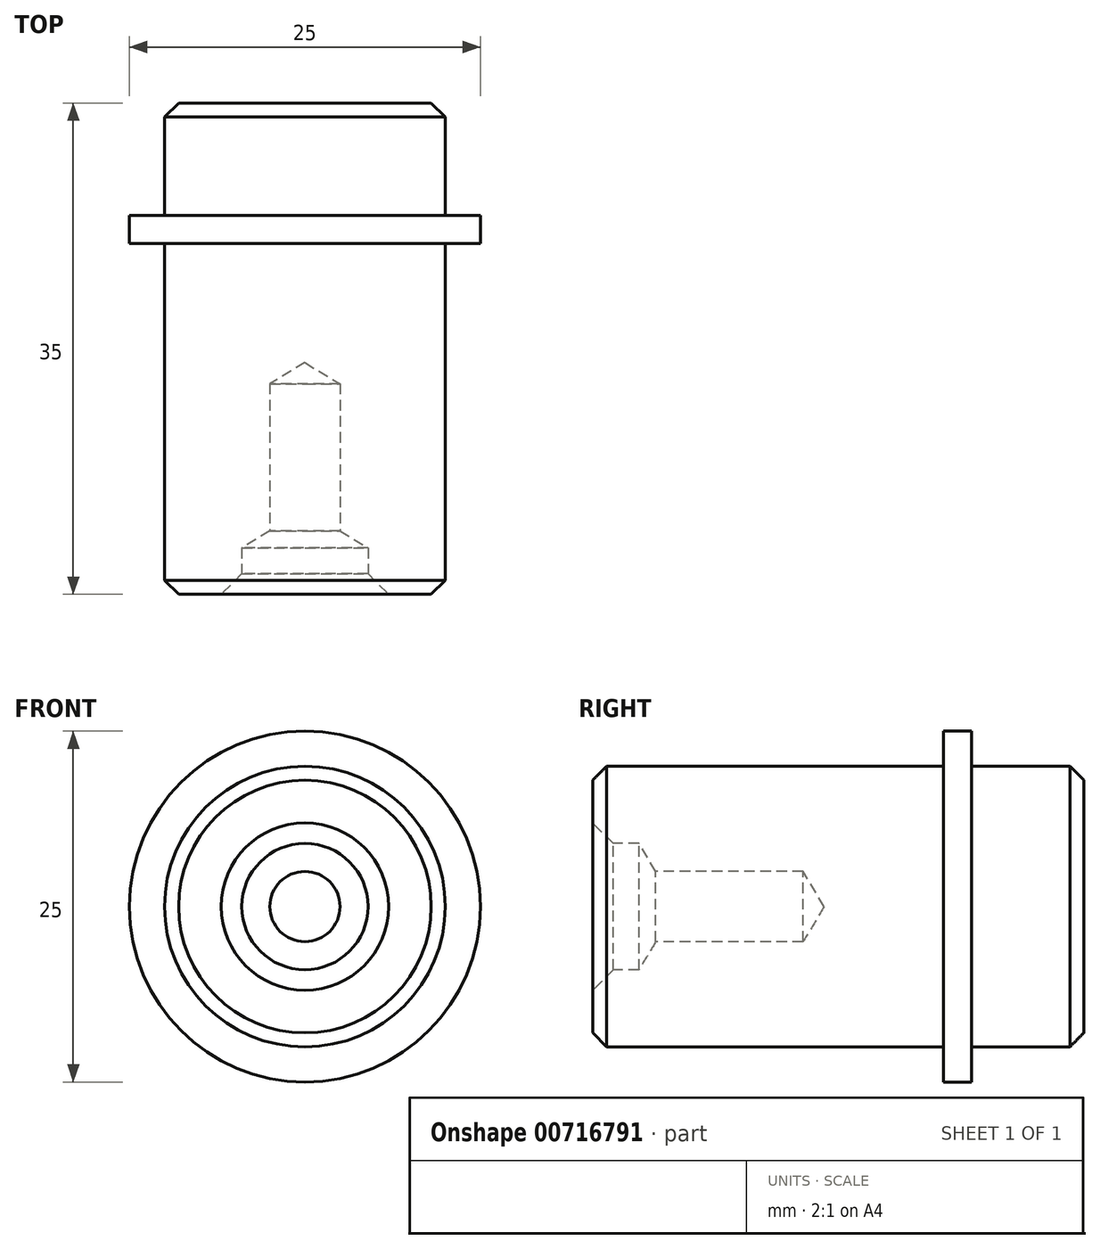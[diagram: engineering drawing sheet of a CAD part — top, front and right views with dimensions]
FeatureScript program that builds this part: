
annotation { "Feature Type Name" : "Feature", "Feature Type Description" : "" }
export const myFeature = defineFeature(function(context is Context, id is Id, definition is map)
    precondition{}
    {
        {
            var Q0;
            Q0=qCreatedBy(makeId("Right.planeOp"),FACE);
            var sketch = newSketch(context, id + "F0", { "sketchPlane" : qUnion([Q0])});
            skLineSegment(sketch, "E0", {"start": v(-17.5, 0) * mm, "end": v(17.5, 0) * mm});
            skLineSegment(sketch, "E1", {"start": v(17.5, 0) * mm, "end": v(17.5, 10) * mm});
            skLineSegment(sketch, "E2", {"start": v(17.5, 10) * mm, "end": v(9.5, 10) * mm});
            skLineSegment(sketch, "E3", {"start": v(9.5, 10) * mm, "end": v(9.5, 12.5) * mm});
            skLineSegment(sketch, "E4", {"start": v(9.5, 12.5) * mm, "end": v(7.5, 12.5) * mm});
            skLineSegment(sketch, "E5", {"start": v(7.5, 12.5) * mm, "end": v(7.5, 10) * mm});
            skLineSegment(sketch, "E6", {"start": v(7.5, 10) * mm, "end": v(-17.5, 10) * mm});
            skLineSegment(sketch, "E7", {"start": v(-17.5, 10) * mm, "end": v(-17.5, 0) * mm});
            skSolve(sketch);
        }
        {
            var Q0;
            Q0=makeQuery(id+"F0.imprint","IMPRINT",FACE,{"disambiguationData":[TD([[makeQuery(id+"F0.imprint","IMPRINT",EDGE,{"derivedFrom":sQuery(id+"F0.wireOp",EDGE,"E0")}),1.0]])]});
            var Q1;
            Q1=sQuery(id+"F0.wireOp",EDGE,"E0");
            revolve(context, id + "F1", {"surfaceOperationType" : NewSurfaceOperationType.NEW, "entities" : qUnion([Q0]), "axis" : qUnion([Q1]), "revolveType" : RevolveType.FULL});
        }
        {
            var Q0;
            Q0=makeQuery(id+"F1.opRevolve","SWEPT_EDGE",EDGE,{"disambiguationData":[OSD([sQuery(id+"F0.wireOp",EDGE,"E1"),sQuery(id+"F0.wireOp",EDGE,"E2")])]});
            var Q1;
            Q1=makeQuery(id+"F1.opRevolve","SWEPT_EDGE",EDGE,{"disambiguationData":[OSD([sQuery(id+"F0.wireOp",EDGE,"E6"),sQuery(id+"F0.wireOp",EDGE,"E7")])]});
            chamfer(context, id + "F2", {"entities" : qUnion([Q0, Q1]), "width" : 1 * mm, "tangentPropagation" : true});
        }
        {
            var Q0;
            Q0=makeQuery(id+"F1.opRevolve","SWEPT_FACE",FACE,{"disambiguationData":[OSD([sQuery(id+"F0.wireOp",EDGE,"E7")])]});
            var sketch = newSketch(context, id + "F3", { "sketchPlane" : qUnion([Q0])});
            skPoint(sketch, "E8", {"position": v(0, 0) * mm});
            skSolve(sketch);
        }
        {
            var Q0;
            Q0=sQuery(id+"F3.wireOp",VERTEX,"E8");
            var Q1;
            Q1=makeQuery(id+"F1.opRevolve","SWEPT_BODY",BODY,{"disambiguationData":[OSD([sQuery(id+"F0.wireOp",EDGE,"E0"),sQuery(id+"F0.wireOp",EDGE,"E1"),sQuery(id+"F0.wireOp",EDGE,"E2"),sQuery(id+"F0.wireOp",EDGE,"E3"),sQuery(id+"F0.wireOp",EDGE,"E4"),sQuery(id+"F0.wireOp",EDGE,"E5"),sQuery(id+"F0.wireOp",EDGE,"E6"),sQuery(id+"F0.wireOp",EDGE,"E7")])]});
            hole(context, id + "F4", {"style" : HoleStyle.SIMPLE, "endStyle" : HoleEndStyle.BLIND, "standardTappedOrClearance" : lookupTablePath({ "standard" : "ISO", "engagement" : "75%", "pitch" : "1 mm", "size" : "M6", "type" : "Tapped" }), "standardBlindInLast" : lookupTablePath({ "standard" : "ISO", "engagement" : "75%", "pitch" : "1 mm", "size" : "M6", "type" : "Tapped" }), "holeDiameter" : 5 * mm, "majorDiameter" : 6 * mm, "showTappedDepth" : true, "holeDepth" : 15 * mm, "isTappedThrough" : true, "tappedDepth" : 12 * mm, "tapClearance" : 3, "startFromSketch" : true, "locations" : qUnion([Q0]), "scope" : qUnion([Q1])});
        }
        {
            var Q0;
            Q0=makeQuery(id+"F1.opRevolve","SWEPT_FACE",FACE,{"disambiguationData":[OSD([sQuery(id+"F0.wireOp",EDGE,"E7")])]});
            cPlane(context, id + "F5", {"entities" : qUnion([Q0]), "cplaneType" : CPlaneType.OFFSET, "offset" : 3 * mm, "width" : 150 * mm, "height" : 150 * mm});
        }
        {
            var Q0;
            Q0=qCreatedBy(id+"F5.planeOp",FACE);
            var sketch = newSketch(context, id + "F6", { "sketchPlane" : qUnion([Q0])});
            skPoint(sketch, "E9", {"position": v(0, 0) * mm});
            skSolve(sketch);
        }
        {
            var Q0;
            Q0=sQuery(id+"F6.wireOp",VERTEX,"E9");
            var Q1;
            Q1=makeQuery(id+"F1.opRevolve","SWEPT_BODY",BODY,{"disambiguationData":[OSD([sQuery(id+"F0.wireOp",EDGE,"E0"),sQuery(id+"F0.wireOp",EDGE,"E1"),sQuery(id+"F0.wireOp",EDGE,"E2"),sQuery(id+"F0.wireOp",EDGE,"E3"),sQuery(id+"F0.wireOp",EDGE,"E4"),sQuery(id+"F0.wireOp",EDGE,"E5"),sQuery(id+"F0.wireOp",EDGE,"E6"),sQuery(id+"F0.wireOp",EDGE,"E7")])]});
            hole(context, id + "F7", {"style" : HoleStyle.C_SINK, "endStyle" : HoleEndStyle.BLIND, "holeDiameter" : 9 * mm, "cSinkDiameter" : 17.92 * mm, "cSinkAngle" : 90 * degree, "majorDiameter" : 8 * mm, "holeDepth" : 6.3 * mm, "isTappedThrough" : true, "tappedDepth" : 12 * mm, "tapClearance" : 3, "startFromSketch" : true, "locations" : qUnion([Q0]), "scope" : qUnion([Q1])});
        }
    });
